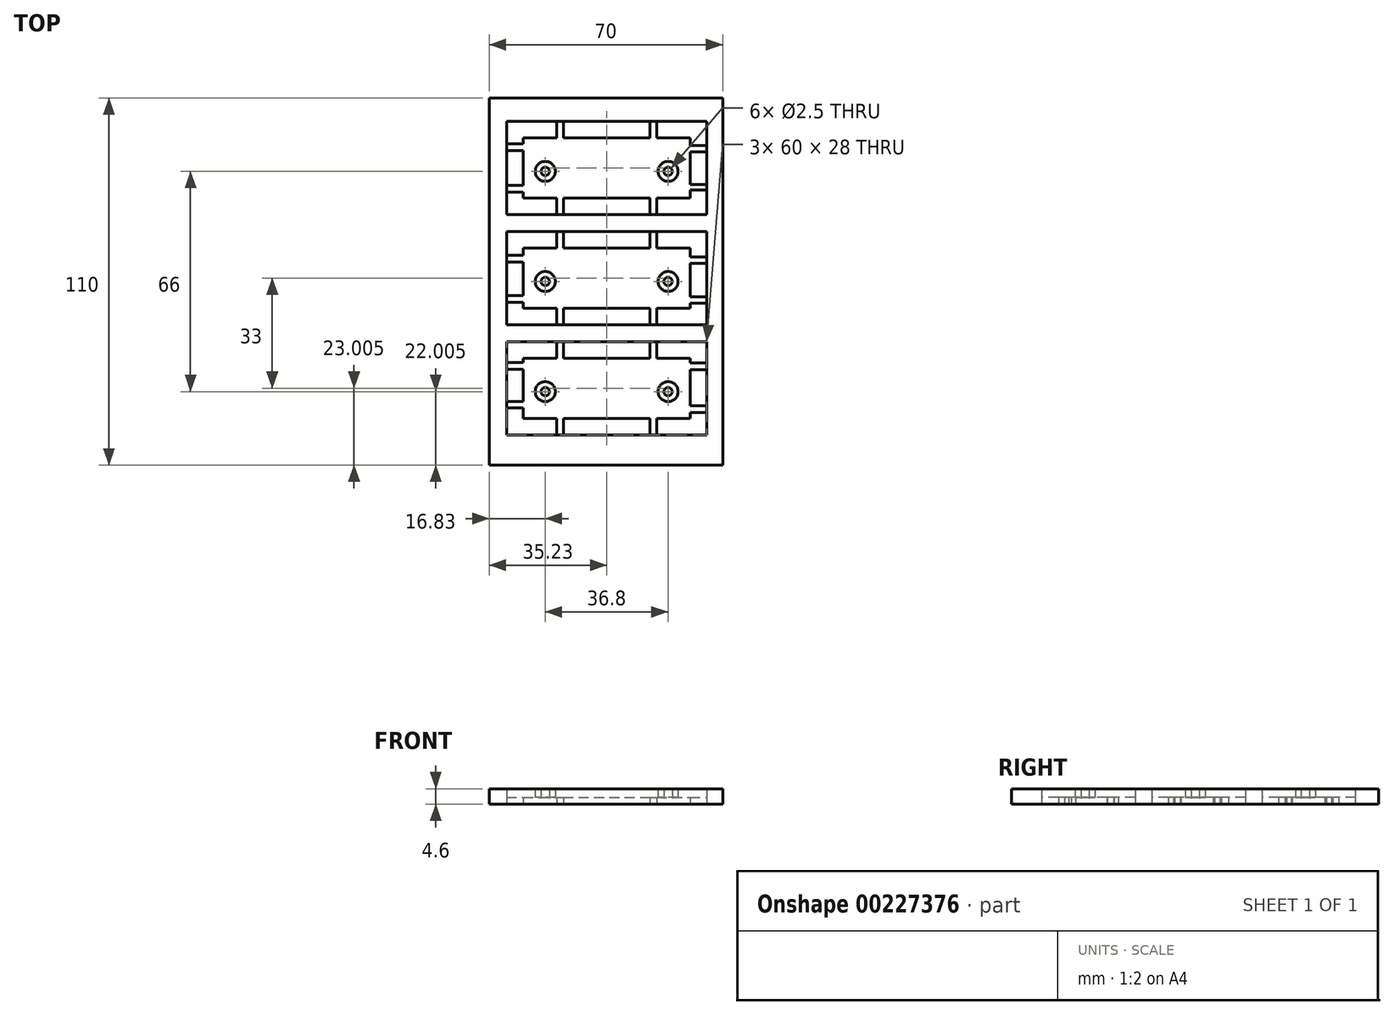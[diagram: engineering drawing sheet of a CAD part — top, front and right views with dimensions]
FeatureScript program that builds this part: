
annotation { "Feature Type Name" : "Feature", "Feature Type Description" : "" }
export const myFeature = defineFeature(function(context is Context, id is Id, definition is map)
    precondition{}
    {
        {
            var Q0;
            Q0=qCreatedBy(makeId("Top.planeOp"),FACE);
            var sketch = newSketch(context, id + "F0", { "sketchPlane" : qUnion([Q0])});
            skLineSegment(sketch, "E0.bottom", {"start": v(-14.26, 31.33) * mm, "end": v(35.74, 31.33) * mm});
            skLineSegment(sketch, "E0.top", {"start": v(-14.26, 13.33) * mm, "end": v(35.74, 13.33) * mm});
            skLineSegment(sketch, "E0.left", {"start": v(-14.26, 31.33) * mm, "end": v(-14.26, 13.33) * mm});
            skLineSegment(sketch, "E0.right", {"start": v(35.74, 31.33) * mm, "end": v(35.74, 13.33) * mm});
            skLineSegment(sketch, "E1.bottom", {"start": v(-14.26, -1.67) * mm, "end": v(35.74, -1.67) * mm});
            skLineSegment(sketch, "E1.top", {"start": v(-14.26, -19.67) * mm, "end": v(35.74, -19.67) * mm});
            skLineSegment(sketch, "E1.left", {"start": v(-14.26, -1.67) * mm, "end": v(-14.26, -19.67) * mm});
            skLineSegment(sketch, "E1.right", {"start": v(35.74, -1.67) * mm, "end": v(35.74, -19.67) * mm});
            skLineSegment(sketch, "E2.bottom", {"start": v(-14.26, -34.67) * mm, "end": v(35.74, -34.67) * mm});
            skLineSegment(sketch, "E2.top", {"start": v(-14.26, -52.67) * mm, "end": v(35.74, -52.67) * mm});
            skLineSegment(sketch, "E2.left", {"start": v(-14.26, -34.67) * mm, "end": v(-14.26, -52.67) * mm});
            skLineSegment(sketch, "E2.right", {"start": v(35.74, -34.67) * mm, "end": v(35.74, -52.67) * mm});
            skLineSegment(sketch, "E3.bottom", {"start": v(-4.26, 31.33) * mm, "end": v(-2.26, 31.33) * mm});
            skLineSegment(sketch, "E3.top", {"start": v(-4.26, 36.33) * mm, "end": v(-2.26, 36.33) * mm});
            skLineSegment(sketch, "E3.left", {"start": v(-4.26, 31.33) * mm, "end": v(-4.26, 36.33) * mm});
            skLineSegment(sketch, "E3.right", {"start": v(-2.26, 31.33) * mm, "end": v(-2.26, 36.33) * mm});
            skLineSegment(sketch, "E4.bottom", {"start": v(23.74, 36.33) * mm, "end": v(25.74, 36.33) * mm});
            skLineSegment(sketch, "E4.top", {"start": v(23.74, 31.33) * mm, "end": v(25.74, 31.33) * mm});
            skLineSegment(sketch, "E4.left", {"start": v(23.74, 36.33) * mm, "end": v(23.74, 31.33) * mm});
            skLineSegment(sketch, "E4.right", {"start": v(25.74, 36.33) * mm, "end": v(25.74, 31.33) * mm});
            skPoint(sketch, "E5.firstSnap0", {"position": v(-4.26, 33.83) * mm});
            skLineSegment(sketch, "E5.bottom", {"start": v(-4.26, 13.33) * mm, "end": v(-2.26, 13.33) * mm});
            skLineSegment(sketch, "E5.top", {"start": v(-4.26, 8.33) * mm, "end": v(-2.26, 8.33) * mm});
            skLineSegment(sketch, "E5.left", {"start": v(-4.26, 13.33) * mm, "end": v(-4.26, 8.33) * mm});
            skLineSegment(sketch, "E5.right", {"start": v(-2.26, 13.33) * mm, "end": v(-2.26, 8.33) * mm});
            skLineSegment(sketch, "E6.bottom", {"start": v(23.74, 13.33) * mm, "end": v(25.74, 13.33) * mm});
            skLineSegment(sketch, "E6.top", {"start": v(23.74, 8.33) * mm, "end": v(25.74, 8.33) * mm});
            skLineSegment(sketch, "E6.left", {"start": v(23.74, 13.33) * mm, "end": v(23.74, 8.33) * mm});
            skLineSegment(sketch, "E6.right", {"start": v(25.74, 13.33) * mm, "end": v(25.74, 8.33) * mm});
            skLineSegment(sketch, "E7.bottom", {"start": v(-4.26, -1.67) * mm, "end": v(-2.26, -1.67) * mm});
            skLineSegment(sketch, "E7.top", {"start": v(-4.26, 3.33) * mm, "end": v(-2.26, 3.33) * mm});
            skLineSegment(sketch, "E7.left", {"start": v(-4.26, -1.67) * mm, "end": v(-4.26, 3.33) * mm});
            skLineSegment(sketch, "E7.right", {"start": v(-2.26, -1.67) * mm, "end": v(-2.26, 3.33) * mm});
            skLineSegment(sketch, "E8.bottom", {"start": v(23.74, 3.33) * mm, "end": v(25.74, 3.33) * mm});
            skLineSegment(sketch, "E8.top", {"start": v(23.74, -1.67) * mm, "end": v(25.74, -1.67) * mm});
            skLineSegment(sketch, "E8.left", {"start": v(23.74, 3.33) * mm, "end": v(23.74, -1.67) * mm});
            skLineSegment(sketch, "E8.right", {"start": v(25.74, 3.33) * mm, "end": v(25.74, -1.67) * mm});
            skLineSegment(sketch, "E9.bottom", {"start": v(-4.26, -19.67) * mm, "end": v(-2.26, -19.67) * mm});
            skLineSegment(sketch, "E9.top", {"start": v(-4.26, -24.67) * mm, "end": v(-2.26, -24.67) * mm});
            skLineSegment(sketch, "E9.left", {"start": v(-4.26, -19.67) * mm, "end": v(-4.26, -24.67) * mm});
            skLineSegment(sketch, "E9.right", {"start": v(-2.26, -19.67) * mm, "end": v(-2.26, -24.67) * mm});
            skLineSegment(sketch, "E10.bottom", {"start": v(23.74, -19.67) * mm, "end": v(25.74, -19.67) * mm});
            skLineSegment(sketch, "E10.top", {"start": v(23.74, -24.67) * mm, "end": v(25.74, -24.67) * mm});
            skLineSegment(sketch, "E10.left", {"start": v(23.74, -19.67) * mm, "end": v(23.74, -24.67) * mm});
            skLineSegment(sketch, "E10.right", {"start": v(25.74, -19.67) * mm, "end": v(25.74, -24.67) * mm});
            skLineSegment(sketch, "E11.bottom", {"start": v(-4.26, -29.67) * mm, "end": v(-2.26, -29.67) * mm});
            skLineSegment(sketch, "E11.top", {"start": v(-4.26, -34.67) * mm, "end": v(-2.26, -34.67) * mm});
            skLineSegment(sketch, "E11.left", {"start": v(-4.26, -29.67) * mm, "end": v(-4.26, -34.67) * mm});
            skLineSegment(sketch, "E11.right", {"start": v(-2.26, -29.67) * mm, "end": v(-2.26, -34.67) * mm});
            skLineSegment(sketch, "E12.bottom", {"start": v(23.74, -29.67) * mm, "end": v(25.74, -29.67) * mm});
            skLineSegment(sketch, "E12.top", {"start": v(23.74, -34.67) * mm, "end": v(25.74, -34.67) * mm});
            skLineSegment(sketch, "E12.left", {"start": v(23.74, -29.67) * mm, "end": v(23.74, -34.67) * mm});
            skLineSegment(sketch, "E12.right", {"start": v(25.74, -29.67) * mm, "end": v(25.74, -34.67) * mm});
            skLineSegment(sketch, "E13.bottom", {"start": v(-4.26, -52.67) * mm, "end": v(-2.26, -52.67) * mm});
            skLineSegment(sketch, "E13.top", {"start": v(-4.26, -57.67) * mm, "end": v(-2.26, -57.67) * mm});
            skLineSegment(sketch, "E13.left", {"start": v(-4.26, -52.67) * mm, "end": v(-4.26, -57.67) * mm});
            skLineSegment(sketch, "E13.right", {"start": v(-2.26, -52.67) * mm, "end": v(-2.26, -57.67) * mm});
            skLineSegment(sketch, "E14.bottom", {"start": v(23.74, -52.67) * mm, "end": v(25.74, -52.67) * mm});
            skLineSegment(sketch, "E14.top", {"start": v(23.74, -57.67) * mm, "end": v(25.74, -57.67) * mm});
            skLineSegment(sketch, "E14.left", {"start": v(23.74, -52.67) * mm, "end": v(23.74, -57.67) * mm});
            skLineSegment(sketch, "E14.right", {"start": v(25.74, -52.67) * mm, "end": v(25.74, -57.67) * mm});
            skLineSegment(sketch, "E15.left", {"start": v(-14.26, 22.33) * mm, "end": v(-14.26, 20.33) * mm});
            skLineSegment(sketch, "E16.left", {"start": v(35.74, 22.33) * mm, "end": v(35.74, 20.33) * mm});
            skLineSegment(sketch, "E17.left", {"start": v(35.74, -10.67) * mm, "end": v(35.74, -12.67) * mm});
            skLineSegment(sketch, "E18.left", {"start": v(-14.26, -10.67) * mm, "end": v(-14.26, -12.67) * mm});
            skLineSegment(sketch, "E19.left", {"start": v(35.74, -43.67) * mm, "end": v(35.74, -45.67) * mm});
            skPoint(sketch, "E20.oppositeSnap0", {"position": v(-14.26, -43.67) * mm});
            skLineSegment(sketch, "E20.left", {"start": v(-14.26, -41.67) * mm, "end": v(-14.26, -43.67) * mm});
            skCircle(sketch, "E21", {"center": v(-7.66, 21.33) * mm, "radius": 3 * mm});
            skCircle(sketch, "E22", {"center": v(-7.66, 21.33) * mm, "radius": 1.25 * mm});
            skCircle(sketch, "E23", {"center": v(29.14, 21.33) * mm, "radius": 3 * mm});
            skCircle(sketch, "E24", {"center": v(29.14, 21.33) * mm, "radius": 1.25 * mm});
            skCircle(sketch, "E25", {"center": v(-7.66, -11.67) * mm, "radius": 3 * mm});
            skCircle(sketch, "E26", {"center": v(-7.66, -11.67) * mm, "radius": 1.25 * mm});
            skCircle(sketch, "E27", {"center": v(29.14, -11.67) * mm, "radius": 3 * mm});
            skCircle(sketch, "E28", {"center": v(29.14, -11.67) * mm, "radius": 1.25 * mm});
            skCircle(sketch, "E29", {"center": v(-7.66, -44.67) * mm, "radius": 3 * mm});
            skCircle(sketch, "E30", {"center": v(-7.66, -44.67) * mm, "radius": 1.25 * mm});
            skCircle(sketch, "E31", {"center": v(29.14, -44.67) * mm, "radius": 3 * mm});
            skCircle(sketch, "E32", {"center": v(29.14, -44.67) * mm, "radius": 1.25 * mm});
            skLineSegment(sketch, "E33.top", {"start": v(8.74, 31.33) * mm, "end": v(10.74, 31.33) * mm});
            skLineSegment(sketch, "E34.bottom", {"start": v(8.74, 13.33) * mm, "end": v(10.74, 13.33) * mm});
            skLineSegment(sketch, "E35.top", {"start": v(8.74, -1.67) * mm, "end": v(10.74, -1.67) * mm});
            skLineSegment(sketch, "E36.bottom", {"start": v(8.78, -19.67) * mm, "end": v(10.78, -19.67) * mm});
            skLineSegment(sketch, "E37.top", {"start": v(8.74, -34.67) * mm, "end": v(10.74, -34.67) * mm});
            skLineSegment(sketch, "E38.bottom", {"start": v(8.3, -52.67) * mm, "end": v(10.3, -52.67) * mm});
            skLineSegment(sketch, "E39.bottom", {"start": v(-19.26, -15.88) * mm, "end": v(-14.26, -15.88) * mm});
            skLineSegment(sketch, "E39.top", {"start": v(-19.26, -17.87) * mm, "end": v(-14.26, -17.87) * mm});
            skLineSegment(sketch, "E39.left", {"start": v(-19.26, -15.88) * mm, "end": v(-19.26, -17.87) * mm});
            skLineSegment(sketch, "E39.right", {"start": v(-14.26, -15.88) * mm, "end": v(-14.26, -17.87) * mm});
            skLineSegment(sketch, "E40.bottom", {"start": v(-19.26, -3.86) * mm, "end": v(-14.26, -3.86) * mm});
            skLineSegment(sketch, "E40.top", {"start": v(-19.26, -5.86) * mm, "end": v(-14.26, -5.86) * mm});
            skLineSegment(sketch, "E40.left", {"start": v(-19.26, -3.86) * mm, "end": v(-19.26, -5.86) * mm});
            skLineSegment(sketch, "E40.right", {"start": v(-14.26, -3.86) * mm, "end": v(-14.26, -5.86) * mm});
            skLineSegment(sketch, "E41.bottom", {"start": v(35.74, -4.26) * mm, "end": v(40.74, -4.26) * mm});
            skLineSegment(sketch, "E41.top", {"start": v(35.74, -6.26) * mm, "end": v(40.74, -6.26) * mm});
            skLineSegment(sketch, "E41.left", {"start": v(35.74, -4.26) * mm, "end": v(35.74, -6.26) * mm});
            skLineSegment(sketch, "E41.right", {"start": v(40.74, -4.26) * mm, "end": v(40.74, -6.26) * mm});
            skLineSegment(sketch, "E42.bottom", {"start": v(35.74, -16.2) * mm, "end": v(40.74, -16.2) * mm});
            skLineSegment(sketch, "E42.top", {"start": v(35.74, -18.2) * mm, "end": v(40.74, -18.2) * mm});
            skLineSegment(sketch, "E42.left", {"start": v(35.74, -16.2) * mm, "end": v(35.74, -18.2) * mm});
            skLineSegment(sketch, "E42.right", {"start": v(40.74, -16.2) * mm, "end": v(40.74, -18.2) * mm});
            skLineSegment(sketch, "E43.bottom", {"start": v(35.74, 29.13) * mm, "end": v(40.74, 29.13) * mm});
            skLineSegment(sketch, "E43.top", {"start": v(35.74, 27.12) * mm, "end": v(40.74, 27.12) * mm});
            skLineSegment(sketch, "E43.left", {"start": v(35.74, 29.13) * mm, "end": v(35.74, 27.12) * mm});
            skLineSegment(sketch, "E43.right", {"start": v(40.74, 29.13) * mm, "end": v(40.74, 27.12) * mm});
            skLineSegment(sketch, "E44.bottom", {"start": v(35.74, 17.34) * mm, "end": v(40.74, 17.34) * mm});
            skLineSegment(sketch, "E44.top", {"start": v(35.74, 15.76) * mm, "end": v(40.74, 15.76) * mm});
            skLineSegment(sketch, "E44.left", {"start": v(35.74, 17.34) * mm, "end": v(35.74, 15.76) * mm});
            skLineSegment(sketch, "E44.right", {"start": v(40.74, 17.34) * mm, "end": v(40.74, 15.76) * mm});
            skLineSegment(sketch, "E45.bottom", {"start": v(-19.26, -47.57) * mm, "end": v(-14.26, -47.57) * mm});
            skLineSegment(sketch, "E45.top", {"start": v(-19.26, -49.57) * mm, "end": v(-14.26, -49.57) * mm});
            skLineSegment(sketch, "E45.left", {"start": v(-19.26, -47.57) * mm, "end": v(-19.26, -49.57) * mm});
            skLineSegment(sketch, "E45.right", {"start": v(-14.26, -47.57) * mm, "end": v(-14.26, -49.57) * mm});
            skLineSegment(sketch, "E46.bottom", {"start": v(-19.26, 29.6) * mm, "end": v(-14.26, 29.6) * mm});
            skLineSegment(sketch, "E46.top", {"start": v(-19.26, 27.6) * mm, "end": v(-14.26, 27.6) * mm});
            skLineSegment(sketch, "E46.left", {"start": v(-19.26, 29.6) * mm, "end": v(-19.26, 27.6) * mm});
            skLineSegment(sketch, "E46.right", {"start": v(-14.26, 29.6) * mm, "end": v(-14.26, 27.6) * mm});
            skLineSegment(sketch, "E47.bottom", {"start": v(-19.26, 17.17) * mm, "end": v(-14.26, 17.17) * mm});
            skLineSegment(sketch, "E47.top", {"start": v(-19.26, 15.17) * mm, "end": v(-14.26, 15.17) * mm});
            skLineSegment(sketch, "E47.left", {"start": v(-19.26, 17.17) * mm, "end": v(-19.26, 15.17) * mm});
            skLineSegment(sketch, "E47.right", {"start": v(-14.26, 17.17) * mm, "end": v(-14.26, 15.17) * mm});
            skLineSegment(sketch, "E48.bottom", {"start": v(35.74, -36.08) * mm, "end": v(40.74, -36.08) * mm});
            skLineSegment(sketch, "E48.top", {"start": v(35.74, -38.08) * mm, "end": v(40.74, -38.08) * mm});
            skLineSegment(sketch, "E48.left", {"start": v(35.74, -36.08) * mm, "end": v(35.74, -38.08) * mm});
            skLineSegment(sketch, "E48.right", {"start": v(40.74, -36.08) * mm, "end": v(40.74, -38.08) * mm});
            skLineSegment(sketch, "E49.bottom", {"start": v(35.74, -48.86) * mm, "end": v(40.74, -48.86) * mm});
            skLineSegment(sketch, "E49.top", {"start": v(35.74, -50.86) * mm, "end": v(40.74, -50.86) * mm});
            skLineSegment(sketch, "E49.left", {"start": v(35.74, -48.86) * mm, "end": v(35.74, -50.86) * mm});
            skLineSegment(sketch, "E49.right", {"start": v(40.74, -48.86) * mm, "end": v(40.74, -50.86) * mm});
            skLineSegment(sketch, "E50.bottom", {"start": v(-19.26, -35.96) * mm, "end": v(-14.26, -35.96) * mm});
            skLineSegment(sketch, "E50.top", {"start": v(-19.26, -37.96) * mm, "end": v(-14.26, -37.96) * mm});
            skLineSegment(sketch, "E50.left", {"start": v(-19.26, -35.96) * mm, "end": v(-19.26, -37.96) * mm});
            skLineSegment(sketch, "E50.right", {"start": v(-14.26, -35.96) * mm, "end": v(-14.26, -37.96) * mm});
            skSolve(sketch);
        }
        {
            var Q0;
            Q0=qSketchRegion(id+"F0",true);
            extrude(context, id + "F1", {"entities" : qUnion([Q0]), "depth" : 2 * mm});
        }
        {
            var Q0;
            Q0=qCreatedBy(makeId("Top.planeOp"),FACE);
            var sketch = newSketch(context, id + "F2", { "sketchPlane" : qUnion([Q0])});
            skLineSegment(sketch, "E51.bottom", {"start": v(-19.26, 36.33) * mm, "end": v(40.74, 36.33) * mm});
            skLineSegment(sketch, "E51.top", {"start": v(-19.26, 8.33) * mm, "end": v(40.74, 8.33) * mm});
            skLineSegment(sketch, "E51.left", {"start": v(-19.26, 36.33) * mm, "end": v(-19.26, 8.33) * mm});
            skLineSegment(sketch, "E51.right", {"start": v(40.74, 36.33) * mm, "end": v(40.74, 8.33) * mm});
            skLineSegment(sketch, "E52.bottom", {"start": v(-19.26, 3.33) * mm, "end": v(40.74, 3.33) * mm});
            skLineSegment(sketch, "E52.top", {"start": v(-19.26, -24.67) * mm, "end": v(40.74, -24.67) * mm});
            skLineSegment(sketch, "E52.left", {"start": v(-19.26, 3.33) * mm, "end": v(-19.26, -24.67) * mm});
            skLineSegment(sketch, "E52.right", {"start": v(40.74, 3.33) * mm, "end": v(40.74, -24.67) * mm});
            skLineSegment(sketch, "E53.bottom", {"start": v(-19.26, -29.67) * mm, "end": v(40.74, -29.67) * mm});
            skLineSegment(sketch, "E53.top", {"start": v(-19.26, -57.67) * mm, "end": v(40.74, -57.67) * mm});
            skLineSegment(sketch, "E53.left", {"start": v(-19.26, -29.67) * mm, "end": v(-19.26, -57.67) * mm});
            skLineSegment(sketch, "E53.right", {"start": v(40.74, -29.67) * mm, "end": v(40.74, -57.67) * mm});
            skLineSegment(sketch, "E54.bottom", {"start": v(-24.5, 43.33) * mm, "end": v(45.5, 43.33) * mm});
            skLineSegment(sketch, "E54.top", {"start": v(-24.5, -66.67) * mm, "end": v(45.5, -66.67) * mm});
            skLineSegment(sketch, "E54.left", {"start": v(-24.5, 43.33) * mm, "end": v(-24.5, -66.67) * mm});
            skLineSegment(sketch, "E54.right", {"start": v(45.5, 43.33) * mm, "end": v(45.5, -66.67) * mm});
            skSolve(sketch);
        }
        {
            var Q0;
            Q0 = qSketchRegion(id + "F2", true);
            extrude(context, id + "F3", {"entities" : qUnion([Q0]), "depth" : 4.6 * mm, "offsetDistance" : 25 * mm});
        }
        {
            var Q0;
            Q0=makeQuery(id+"F0.imprint","IMPRINT",FACE,{"disambiguationData":[TD([[makeQuery(id+"F0.imprint","IMPRINT",EDGE,{"derivedFrom":sQuery(id+"F0.wireOp",EDGE,"E21")}),1.0]])]});
            var Q1;
            Q1=makeQuery(id+"F0.imprint","IMPRINT",FACE,{"disambiguationData":[TD([[makeQuery(id+"F0.imprint","IMPRINT",EDGE,{"derivedFrom":sQuery(id+"F0.wireOp",EDGE,"E23")}),1.0]])]});
            var Q2;
            Q2=makeQuery(id+"F0.imprint","IMPRINT",FACE,{"disambiguationData":[TD([[makeQuery(id+"F0.imprint","IMPRINT",EDGE,{"derivedFrom":sQuery(id+"F0.wireOp",EDGE,"E25")}),1.0]])]});
            var Q3;
            Q3=makeQuery(id+"F0.imprint","IMPRINT",FACE,{"disambiguationData":[TD([[makeQuery(id+"F0.imprint","IMPRINT",EDGE,{"derivedFrom":sQuery(id+"F0.wireOp",EDGE,"E27")}),1.0]])]});
            var Q4;
            Q4=makeQuery(id+"F0.imprint","IMPRINT",FACE,{"disambiguationData":[TD([[makeQuery(id+"F0.imprint","IMPRINT",EDGE,{"derivedFrom":sQuery(id+"F0.wireOp",EDGE,"E29")}),1.0]])]});
            var Q5;
            Q5=makeQuery(id+"F0.imprint","IMPRINT",FACE,{"disambiguationData":[TD([[makeQuery(id+"F0.imprint","IMPRINT",EDGE,{"derivedFrom":sQuery(id+"F0.wireOp",EDGE,"E31")}),1.0]])]});
            extrude(context, id + "F4", {"entities" : qUnion([Q0, Q1, Q2, Q3, Q4, Q5]), "operationType" : NewBodyOperationType.ADD, "depth" : 4.6 * mm});
        }
    });
